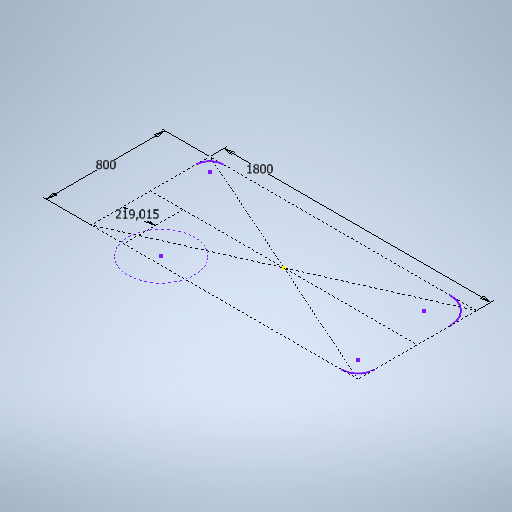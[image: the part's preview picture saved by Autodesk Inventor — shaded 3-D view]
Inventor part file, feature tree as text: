
AUTODESK INVENTOR PART (.ipt)
format: ipt  version: 2025.2 (Build 292293000, 293)  size: 276,480 bytes
history: native  units: mm
features: sketch x2
ambient origin geometry x8: Origin, YZ Plane, XZ Plane, XY Plane, X Axis, Y Axis, Z Axis, Center Point
feature tree (2):
  sketch  "Esboço1"  dims[d0=800.0mm]
  sketch  "Esboço3"  dims[d1=1800.0mm d3=650.0mm d5=15.0mm d6=800.0mm d7=1800.0mm d9=250.0mm d11=800.0mm d13=400.0mm d14=400.0mm d15=400.0mm d16=1800.0mm d17=800.0mm d19=219.015085mm]
